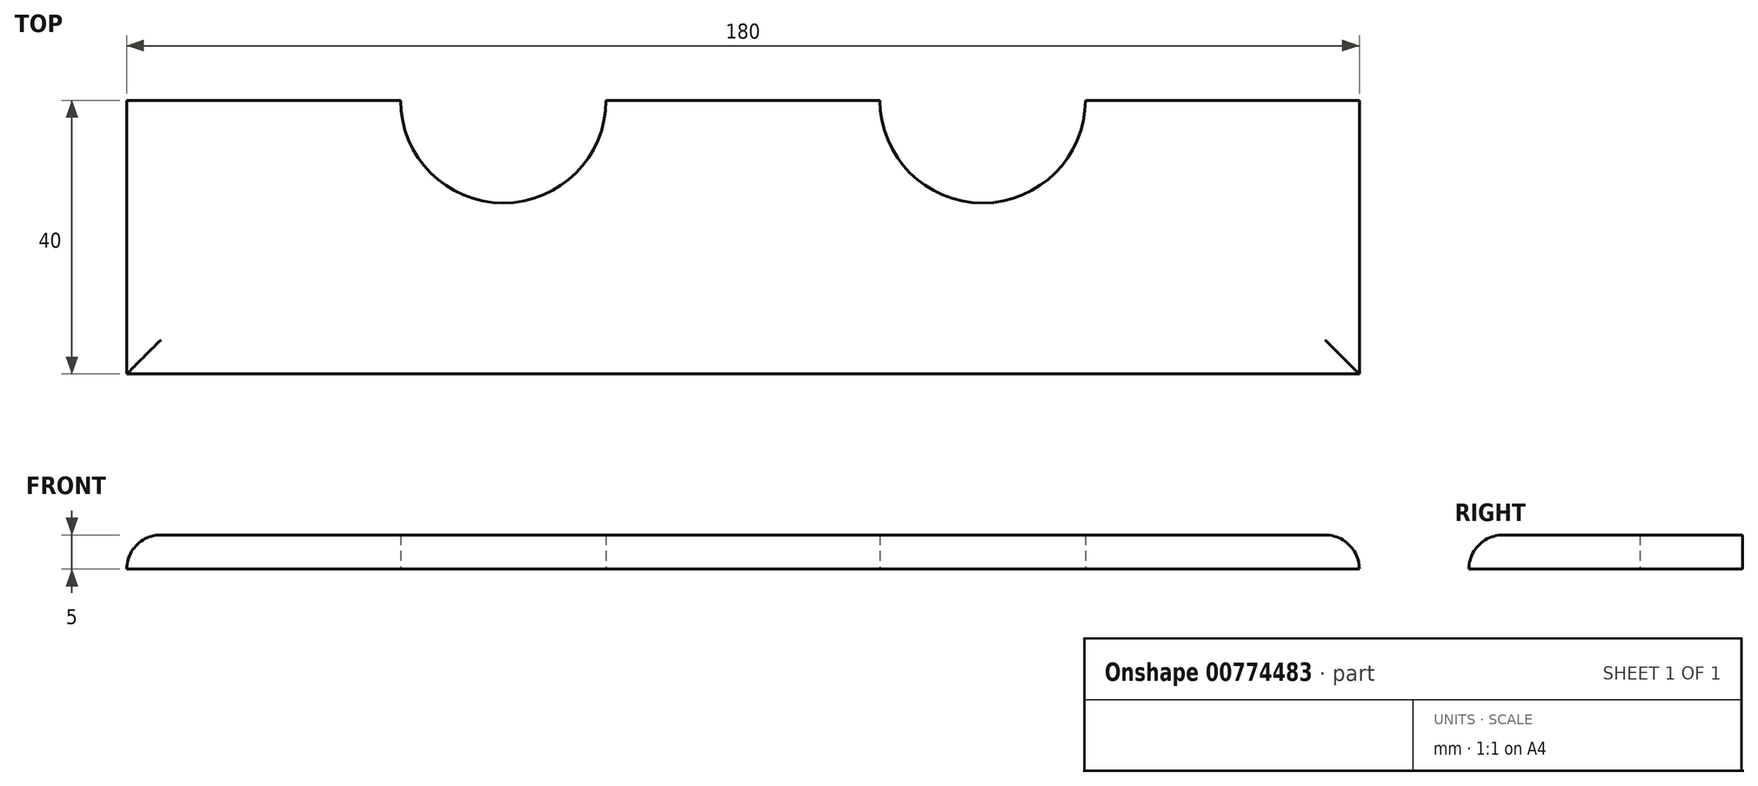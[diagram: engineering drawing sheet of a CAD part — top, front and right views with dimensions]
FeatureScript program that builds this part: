
annotation { "Feature Type Name" : "Feature", "Feature Type Description" : "" }
export const myFeature = defineFeature(function(context is Context, id is Id, definition is map)
    precondition{}
    {
        {
            var Q0;
            Q0=qCreatedBy(makeId("Top.planeOp"),FACE);
            var sketch = newSketch(context, id + "F0", { "sketchPlane" : qUnion([Q0])});
            skLineSegment(sketch, "E0", {"start": v(0, 0) * mm, "end": v(90, 0) * mm});
            skLineSegment(sketch, "E1.bottom", {"start": v(90, 0) * mm, "end": v(0, 0) * mm});
            skLineSegment(sketch, "E1.top", {"start": v(90, -40) * mm, "end": v(0, -40) * mm});
            skLineSegment(sketch, "E1.left", {"start": v(90, 0) * mm, "end": v(90, -40) * mm});
            skLineSegment(sketch, "E1.right", {"start": v(0, 0) * mm, "end": v(0, -40) * mm, "construction": true});
            skLineSegment(sketch, "E2.MirrorCS", {"start": v(-90, 0) * mm, "end": v(0, 0) * mm});
            skLineSegment(sketch, "E3.MirrorCS", {"start": v(-90, 0) * mm, "end": v(-90, -40) * mm});
            skLineSegment(sketch, "E4.MirrorCS", {"start": v(-90, -40) * mm, "end": v(0, -40) * mm});
            skArc(sketch, "E5", {"start": v(20, 0) * mm, "mid": v(35, -15) * mm, "end": v(50, 0) * mm});
            skArc(sketch, "E6.MirrorCS", {"start": v(-20, 0) * mm, "mid": v(-35, -15) * mm, "end": v(-50, 0) * mm});
            skSolve(sketch);
        }
        {
            var Q0;
            Q0=makeQuery(id+"F0.imprint","IMPRINT",FACE,{"disambiguationData":[TD([[makeQuery(id+"F0.imprint","IMPRINT",EDGE,{"derivedFrom":sQuery(id+"F0.wireOp",EDGE,"E1.top")}),-1.0]])]});
            extrude(context, id + "F1", {"entities" : qUnion([Q0]), "depth" : 5 * mm, "offsetDistance" : 25 * mm});
        }
        {
            var Q0;
            Q0=makeQuery(id+"F1.opExtrude","CAP_EDGE",EDGE,{"disambiguationData":[OSD([sQuery(id+"F0.wireOp",EDGE,"E1.top"),sQuery(id+"F0.wireOp",EDGE,"E4.MirrorCS")])],"isStart":false});
            var Q1;
            Q1=makeQuery(id+"F1.opExtrude","CAP_EDGE",EDGE,{"disambiguationData":[OSD([sQuery(id+"F0.wireOp",EDGE,"E3.MirrorCS")])],"isStart":false});
            var Q2;
            Q2=makeQuery(id+"F1.opExtrude","CAP_EDGE",EDGE,{"disambiguationData":[OSD([sQuery(id+"F0.wireOp",EDGE,"E1.left")])],"isStart":false});
            fillet(context, id + "F2", {"entities" : qUnion([Q0, Q1, Q2]), "radius" : 5 * mm, "tangentPropagation" : true, "allowEdgeOverflow" : false});
        }
    });
